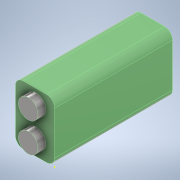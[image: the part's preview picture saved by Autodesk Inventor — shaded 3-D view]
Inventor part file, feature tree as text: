
AUTODESK INVENTOR PART (.ipt)
format: ipt  version: 2021 (Build 250183000, 183)  size: 121,856 bytes
history: native  units: mm
features: sketch x3, extrude x2, fillet x1
ambient origin geometry x8: Origin, YZ Plane, XZ Plane, XY Plane, X Axis, Y Axis, Z Axis, Center Point
bodies: Solid1 (feature_tree)
feature tree (6):
  sketch  "Sketch1"  dims[d0=10.0mm d1=30.0mm d2=15.0mm d3=0.0mm]
  extrude  "Extrusion1"  Depth=30.0mm
  fillet  "Fillet1"  Radius=15.0mm
  extrude  "Extrusion2"  Depth=2.0mm
  sketch  "Sketch2"  dims[d4=2.0mm d5=5.0mm]
  sketch  "Sketch3"  dims[d6=5.0mm d7=2.0mm d8=0.0mm]
